# Revit family: Sink-Kitchen-All_in_One-KOHLER-VAULT-K-80167_1
name_source: partatom
category: Plumbing Fixtures
revit_build: Autodesk Revit 2017 (Build: 20160225_1515(x64)
units: mm (PartAtom-declared; Revit-internal decimal feet)

## family parameters
Cut with Voids When Loaded = No
Host = Face
OmniClass Number = 23.31.13.00
OmniClass Title = Sinks
Part Type = Normal
Room Calculation Point = No
Round Connector Dimension = Use Diameter
Shared = No

## types (1)
- NA-Stainless Steel
    ADA Compliant = No
    Assembly Code = D2010410
    CW Connection = Yes
    Cold Water Inlet = Cold Water Inlet
    Date Modified = 07/30/2021
    Default Elevation = 36"
    Description = All in one Sink Kit
    Drain Included = No
    Finish = Kohler-Metal-NA-Stainless
    HW Connection = Yes
    Handle Clearance = 3 5/8"
    Height = 9"
    Hot Water Inlet = Hot Water Inlet
    Length = 20"
    Manufacturer = KOHLER Co.
    Master Format 2014 = 22 41 16
    Master Format 2014 Name = Residential Lavatories and Sinks
    Material = Stainless Steel
    Model = K-80167-1PC-NA
    Product Documentation Link = https://www.us.kohler.com
    Product Name = Vault
    Product Page URL = http://www.us.kohler.com
    Spout Reach = 8 13/16"
    Type = 1
    URL = https://www.us.kohler.com
    Vent Connection = No
    Waste Connection = Yes
    Waste Water Outlet 1 = Waste Water Outlet 1
    Waste Water Outlet 2 = Waste Water Outlet  2
    WaterSense Certified = No
    Width = 30 1/2"

## geometry (parser evidence)
native form markers: Sweep x7
no freeform markers — native parametric forms only
